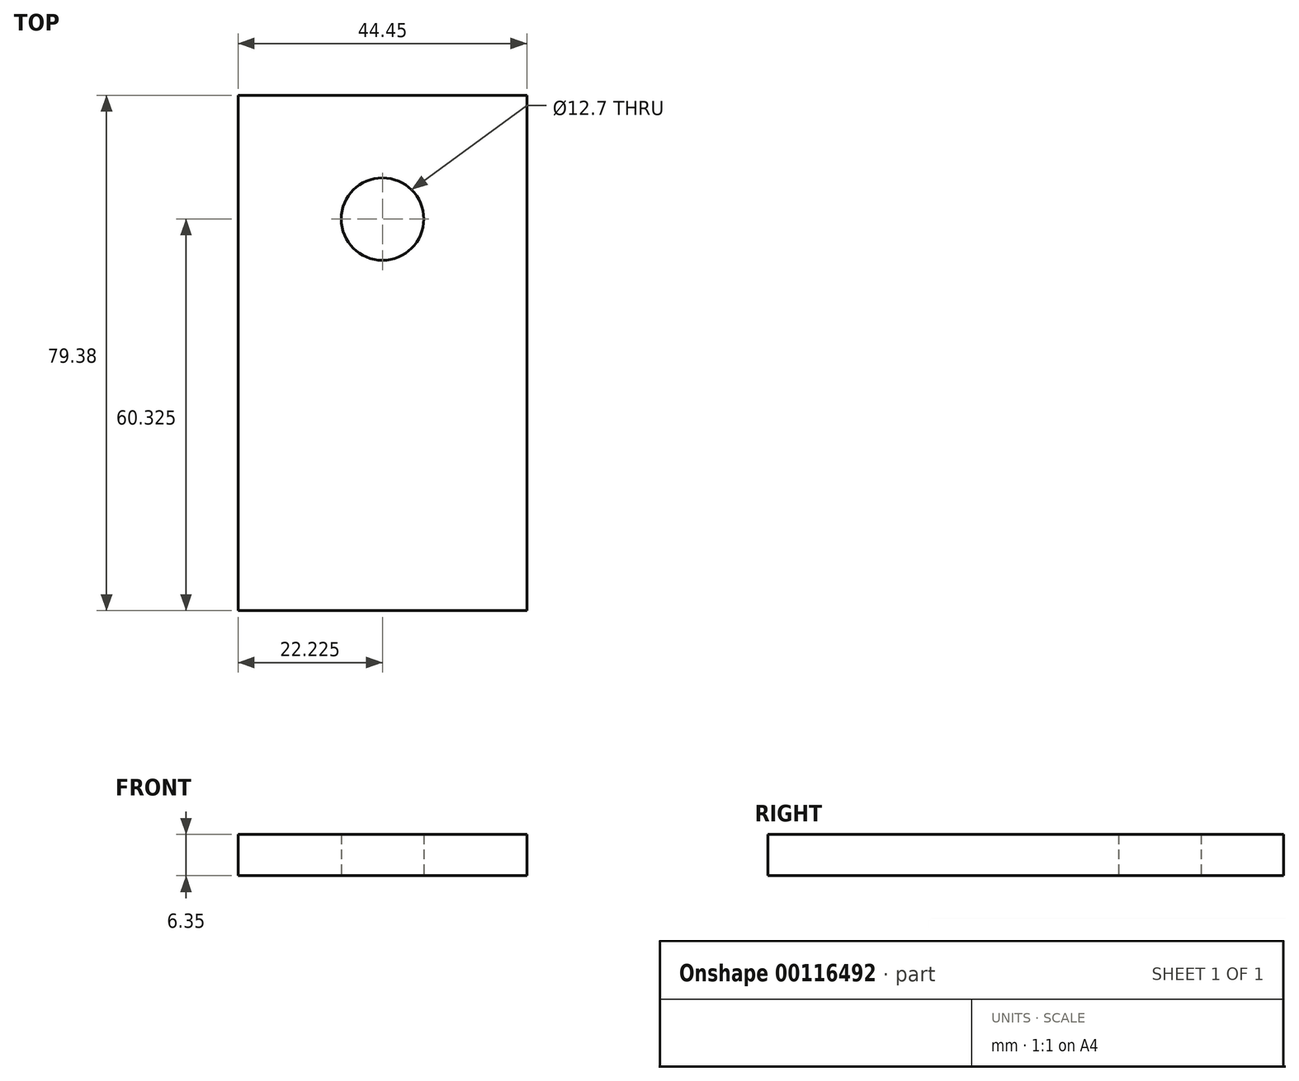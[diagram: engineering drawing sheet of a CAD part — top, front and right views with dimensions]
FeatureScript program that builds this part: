
annotation { "Feature Type Name" : "Feature", "Feature Type Description" : "" }
export const myFeature = defineFeature(function(context is Context, id is Id, definition is map)
    precondition{}
    {
        {
            var Q0;
            Q0=qCreatedBy(makeId("Top.planeOp"),FACE);
            var sketch = newSketch(context, id + "F0", { "sketchPlane" : qUnion([Q0])});
            skLineSegment(sketch, "E0.bottom", {"start": v(0, 0) * mm, "end": v(44.45, 0) * mm});
            skLineSegment(sketch, "E0.top", {"start": v(0, 79.38) * mm, "end": v(44.45, 79.38) * mm});
            skLineSegment(sketch, "E0.left", {"start": v(0, 0) * mm, "end": v(0, 79.38) * mm});
            skLineSegment(sketch, "E0.right", {"start": v(44.45, 0) * mm, "end": v(44.45, 79.38) * mm});
            skCircle(sketch, "E1", {"center": v(22.22, 60.33) * mm, "radius": 6.35 * mm});
            skSolve(sketch);
        }
        {
            var Q0;
            Q0=makeQuery(id+"F0.imprint","IMPRINT",FACE,{"disambiguationData":[TD([[makeQuery(id+"F0.imprint","IMPRINT",EDGE,{"derivedFrom":sQuery(id+"F0.wireOp",EDGE,"E0.bottom")}),1.0]])]});
            extrude(context, id + "F1", {"entities" : qUnion([Q0]), "depth" : 6.35 * mm});
        }
    });
